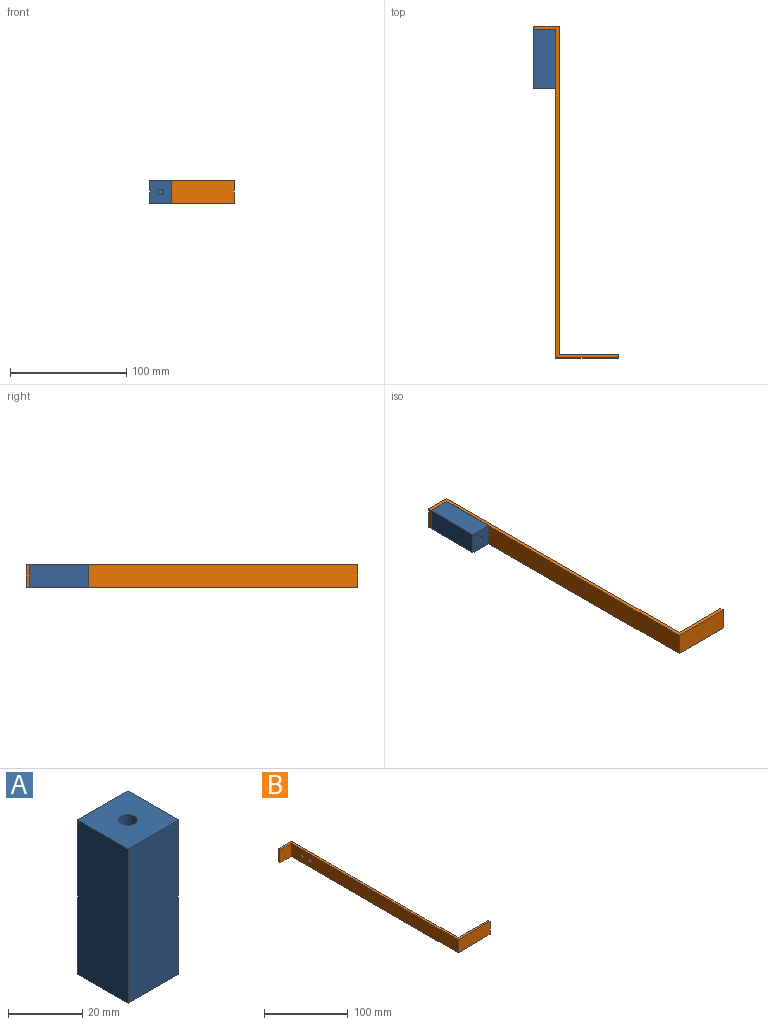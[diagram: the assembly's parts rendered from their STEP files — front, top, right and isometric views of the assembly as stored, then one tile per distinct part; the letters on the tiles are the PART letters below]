
ASSEMBLY  parts=2 mates=1
PART A: 14 faces, bbox 19.1x19.1x50.8 mm
  f0: plane 19.05x19.05mm, normal (0,0,1), area 343.4mm2, adj f1,f3,f4,f5,f6
  f1: plane 50.8x19.05mm, normal (-1,0,0), area 967.7mm2, adj f0,f2,f4,f5
  f2: plane 19.05x19.05mm, normal (0,0,-1), area 343.4mm2, adj f1,f3,f4,f5,f8
  f3: plane 50.8x19.05mm, normal (1,0,0), area 928.8mm2, adj f0,f2,f4,f5,f10,f12
  f4: plane 50.8x19.05mm, normal (0,-1,0), area 967.7mm2, adj f0,f1,f2,f3
  f5: plane 50.8x19.05mm, normal (0,1,0), area 967.7mm2, adj f0,f1,f2,f3
  f6: cylinder r=2.49mm len=12.7mm, axis (0,0,1), area 198.6mm2, adj f0,f7
  f7: plane 4.98x4.98mm, normal (0,0,1), area 19.5mm2, adj f6
  f8: cylinder r=2.49mm len=12.7mm, axis (0,0,-1), area 198.6mm2, adj f2,f9
  f9: plane 4.98x4.98mm, normal (0,0,-1), area 19.5mm2, adj f8
  f10: cylinder r=2.49mm len=12.7mm, axis (1,0,0), area 198.6mm2, adj f3,f11
  f11: plane 4.98x4.98mm, normal (1,0,0), area 19.5mm2, adj f10
  f12: cylinder r=2.49mm len=12.7mm, axis (1,0,0), area 198.6mm2, adj f3,f13
  f13: plane 4.98x4.98mm, normal (1,0,0), area 19.5mm2, adj f12
PART B: 12 faces, bbox 73x285.8x19.1 mm
  f0: plane 19.05x3.18mm, normal (1,0,0), area 60.5mm2, adj f1,f2,f3,f9
  f1: plane 53.98x19.05mm, normal (0,-1,0), area 1028.2mm2, adj f0,f2,f3,f7
  f2: plane 285.75x73.03mm, normal (0,0,1), area 1129mm2, adj f0,f1,f4,f5,f6,f7,f8,f9
  f3: plane 285.75x73.03mm, normal (0,0,-1), area 1129mm2, adj f0,f1,f4,f5,f6,f7,f8,f9
  f4: plane 22.23x19.05mm, normal (0,1,0), area 423.4mm2, adj f2,f3,f5,f8
  f5: plane 19.05x3.18mm, normal (-1,0,0), area 60.5mm2, adj f2,f3,f4,f6
  f6: plane 19.05x19.05mm, normal (0,-1,0), area 362.9mm2, adj f2,f3,f5,f7
  f7: plane 282.58x19.05mm, normal (-1,0,0), area 5344.1mm2, adj f1,f2,f3,f6,f10,f11
  f8: plane 282.58x19.05mm, normal (1,0,0), area 5344.1mm2, adj f2,f3,f4,f9,f10,f11
  f9: plane 50.8x19.05mm, normal (0,1,0), area 967.7mm2, adj f0,f2,f3,f8
  f10: cylinder r=2.49mm len=4.98mm, axis (1,0,0), area 49.7mm2, adj f7,f8
  f11: cylinder r=2.49mm len=4.98mm, axis (1,0,0), area 49.7mm2, adj f7,f8
PLACE A rot(axis=(-1,0,0),90deg) t=(-12.82,150.42,27.87)mm
PLACE B t=(-7.71,-60.82,27.87)mm
MATE fastened A.f10 <-> B.f11  axis (1,0,0) through (-5.37,152.56,37.4)mm
